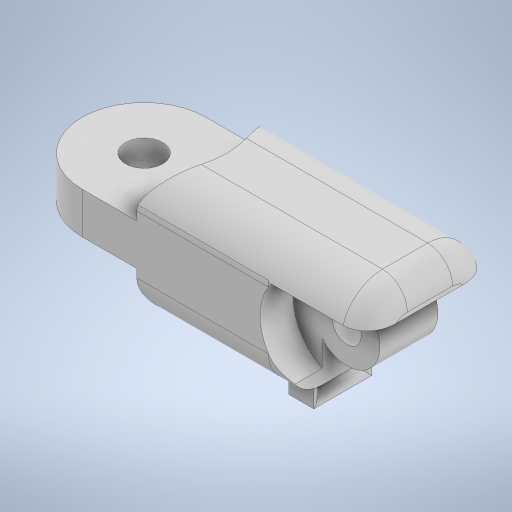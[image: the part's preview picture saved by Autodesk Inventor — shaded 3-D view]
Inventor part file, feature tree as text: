
AUTODESK INVENTOR PART (.ipt)
format: ipt  version: 2024 (Build 280153000, 153)  size: 451,584 bytes
history: native  units: mm
features: sketch x17, extrude x16, fillet x4, other x1
ambient origin geometry x8: Origin, YZ Plane, XZ Plane, XY Plane, X Axis, Y Axis, Z Axis, Center Point
bodies: Body1 (feature_tree)
feature tree (38):
  other  "Твердое тело1"
  extrude  "Выдавливание1"  Depth=15.0mm
  extrude  "Выдавливание2"  Depth=25.0mm
  extrude  "Выдавливание3"  Depth=15.0mm TaperAngle=0.0deg
  extrude  "Выдавливание4"  Depth=5.0mm TaperAngle=0.0deg
  extrude  "Выдавливание5"  Depth=5.0mm TaperAngle=0.0deg
  extrude  "Выдавливание6"  Depth=4.5mm
  extrude  "Выдавливание7"  Depth=5.0mm TaperAngle=0.0deg
  sketch  "Эскиз9"
  extrude  "Выдавливание8"  Depth=8.0mm
  extrude  "Выдавливание9"  Depth=3.0mm
  extrude  "Выдавливание10"  Depth=3.5mm
  extrude  "Выдавливание11"  TaperAngle=0.0deg  [1 undecoded]
  fillet  "Сопряжение6"  Radius=20.0mm
  extrude  "Выдавливание12"  Depth=5.0mm TaperAngle=0.0deg
  extrude  "Выдавливание13"  Depth=20.0mm
  fillet  "Сопряжение7"  Radius=5.0mm
  extrude  "Выдавливание14"  Depth=4.0mm
  extrude  "Выдавливание15"  Depth=0.0mm
  fillet  "Сопряжение8"  [1 undecoded]
  fillet  "Сопряжение9"  Radius=10.0mm
  extrude  "Выдавливание16"  Depth=13.0mm
  sketch  "Эскиз1"
  sketch  "Эскиз2"
  sketch  "Эскиз3"
  sketch  "Эскиз4"
  sketch  "Эскиз6"
  sketch  "Эскиз7"
  sketch  "Эскиз8"
  sketch  "Эскиз10"
  sketch  "Эскиз12"
  sketch  "Эскиз13"
  sketch  "Эскиз14"
  sketch  "Эскиз15"
  sketch  "Эскиз16"
  sketch  "Эскиз17"
  sketch  "Эскиз18"
  sketch  "Эскиз19"
note: 2 required parameter values undecoded (feature->parameter linkage not recoverable at this tier; creation-order binding heuristic only, values carry confidence <= 0.55)
